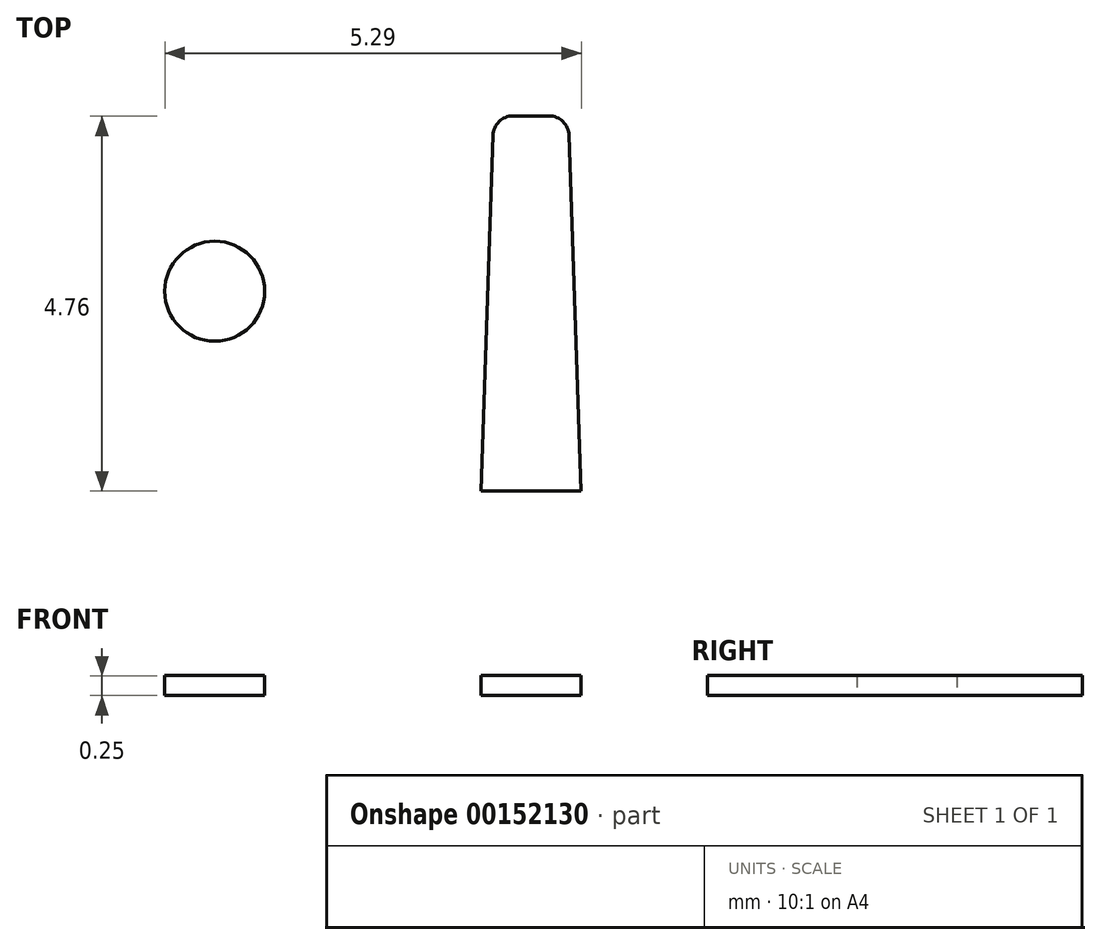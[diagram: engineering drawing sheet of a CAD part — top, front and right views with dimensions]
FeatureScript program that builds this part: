
annotation { "Feature Type Name" : "Feature", "Feature Type Description" : "" }
export const myFeature = defineFeature(function(context is Context, id is Id, definition is map)
    precondition{}
    {
        {
            var Q0;
            Q0=qCreatedBy(makeId("Top.planeOp"),FACE);
            var sketch = newSketch(context, id + "F0", { "sketchPlane" : qUnion([Q0])});
            skLineSegment(sketch, "E0", {"start": v(-0.64, 0) * mm, "end": v(0.64, 0) * mm});
            skLineSegment(sketch, "E1", {"start": v(0.64, 0) * mm, "end": v(0.48, 4.52) * mm});
            skLineSegment(sketch, "E2", {"start": v(-0.63, 0) * mm, "end": v(-0.48, 4.52) * mm});
            skLineSegment(sketch, "E3", {"start": v(-0.23, 4.76) * mm, "end": v(0.23, 4.76) * mm});
            skLineSegment(sketch, "E4", {"start": v(0, 0) * mm, "end": v(0, 4.76) * mm, "construction": true});
            skPoint(sketch, "E5.visualSharp", {"position": v(-0.47, 4.76) * mm});
            skArc(sketch, "E5.filletArc", {"start": v(-0.23, 4.76) * mm, "mid": v(-0.4, 4.7) * mm, "end": v(-0.48, 4.52) * mm});
            skPoint(sketch, "E6.visualSharp", {"position": v(0.47, 4.76) * mm});
            skArc(sketch, "E6.filletArc", {"start": v(0.48, 4.52) * mm, "mid": v(0.4, 4.7) * mm, "end": v(0.23, 4.76) * mm});
            skCircle(sketch, "E7", {"center": v(-4.02, 2.54) * mm, "radius": 0.64 * mm});
            skSolve(sketch);
        }
        {
            var Q0;
            Q0 = qSketchRegion(id + "F0", true);
            extrude(context, id + "F1", {"entities" : qUnion([Q0]), "depth" : 0.25 * mm});
        }
    });
